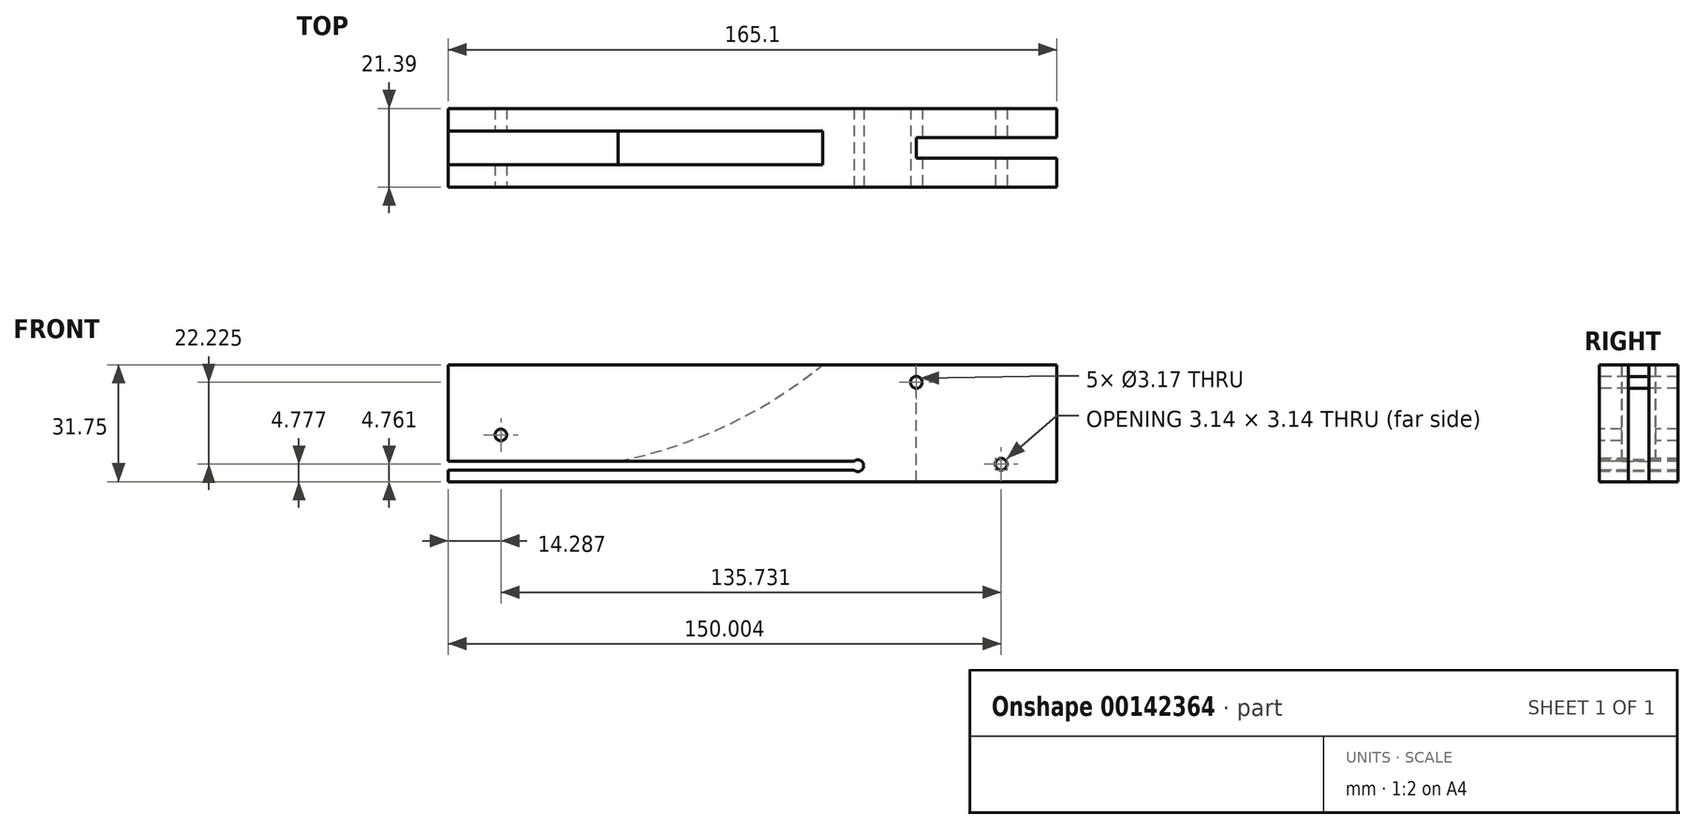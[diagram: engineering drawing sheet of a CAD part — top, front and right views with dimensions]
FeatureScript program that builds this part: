
annotation { "Feature Type Name" : "Feature", "Feature Type Description" : "" }
export const myFeature = defineFeature(function(context is Context, id is Id, definition is map)
    precondition{}
    {
        {
            var Q0;
            Q0=qCreatedBy(makeId("Front.planeOp"),FACE);
            var sketch = newSketch(context, id + "F0", { "sketchPlane" : qUnion([Q0])});
            skPoint(sketch, "E0", {"position": v(-82.55, -12.45) * mm});
            skPoint(sketch, "E1", {"position": v(-57.15, -12.45) * mm});
            skPoint(sketch, "E2", {"position": v(19.05, 16.13) * mm});
            skPoint(sketch, "E3", {"position": v(82.55, 16.13) * mm});
            skPoint(sketch, "E4", {"position": v(82.55, -15.62) * mm});
            skPoint(sketch, "E5", {"position": v(-82.55, -15.62) * mm});
            skLineSegment(sketch, "E6", {"start": v(-82.55, -12.45) * mm, "end": v(-82.55, -15.62) * mm});
            skLineSegment(sketch, "E7", {"start": v(82.55, -15.62) * mm, "end": v(82.55, 16.13) * mm});
            skLineSegment(sketch, "E8", {"start": v(-82.55, -12.45) * mm, "end": v(-57.15, -12.45) * mm});
            skLineSegment(sketch, "E9", {"start": v(-82.55, -15.62) * mm, "end": v(82.55, -15.62) * mm});
            skLineSegment(sketch, "E10", {"start": v(19.05, 16.13) * mm, "end": v(82.55, 16.13) * mm});
            skArc(sketch, "E11", {"start": v(-57.15, -12.45) * mm, "mid": v(-16.7, -4.43) * mm, "end": v(19.05, 16.13) * mm});
            skSolve(sketch);
        }
        {
            var Q0;
            Q0=makeQuery(id+"F0.imprint","IMPRINT",FACE,{"disambiguationData":[TD([[makeQuery(id+"F0.imprint","IMPRINT",EDGE,{"derivedFrom":sQuery(id+"F0.wireOp",EDGE,"E6")}),1.0]])]});
            extrude(context, id + "F1", {"entities" : qUnion([Q0]), "depth" : 9.13 * mm});
        }
        {
            var Q0;
            Q0=makeQuery(id+"F1.opExtrude","CAP_FACE",FACE,{"disambiguationData":[OSD([sQuery(id+"F0.wireOp",EDGE,"E6"),sQuery(id+"F0.wireOp",EDGE,"E7"),sQuery(id+"F0.wireOp",EDGE,"E8"),sQuery(id+"F0.wireOp",EDGE,"E9"),sQuery(id+"F0.wireOp",EDGE,"E10"),sQuery(id+"F0.wireOp",EDGE,"E11")])],"isStart":false});
            var sketch = newSketch(context, id + "F2", { "sketchPlane" : qUnion([Q0])});
            skLineSegment(sketch, "E12", {"start": v(-82.55, -15.62) * mm, "end": v(82.55, -15.62) * mm});
            skLineSegment(sketch, "E13", {"start": v(82.55, -15.62) * mm, "end": v(82.55, 16.13) * mm});
            skLineSegment(sketch, "E14", {"start": v(82.55, 16.13) * mm, "end": v(-82.55, 16.13) * mm});
            skLineSegment(sketch, "E15", {"start": v(-82.55, 16.13) * mm, "end": v(-82.55, -15.62) * mm});
            skSolve(sketch);
        }
        {
            var Q0;
            Q0 = qSketchRegion(id + "F2", true);
            extrude(context, id + "F3", {"entities" : qUnion([Q0]), "operationType" : NewBodyOperationType.ADD, "depth" : 6.13 * mm});
        }
        {
            var Q0;
            Q0=makeQuery(id+"F1.opExtrude","CAP_FACE",FACE,{"disambiguationData":[OSD([sQuery(id+"F0.wireOp",EDGE,"E6"),sQuery(id+"F0.wireOp",EDGE,"E7"),sQuery(id+"F0.wireOp",EDGE,"E8"),sQuery(id+"F0.wireOp",EDGE,"E9"),sQuery(id+"F0.wireOp",EDGE,"E10"),sQuery(id+"F0.wireOp",EDGE,"E11")])],"isStart":true});
            var sketch = newSketch(context, id + "F4", { "sketchPlane" : qUnion([Q0])});
            skLineSegment(sketch, "E16.bottom", {"start": v(-82.55, -15.62) * mm, "end": v(82.55, -15.62) * mm});
            skLineSegment(sketch, "E16.top", {"start": v(-82.55, 16.13) * mm, "end": v(82.55, 16.13) * mm});
            skLineSegment(sketch, "E16.left", {"start": v(-82.55, -15.62) * mm, "end": v(-82.55, 16.13) * mm});
            skLineSegment(sketch, "E16.right", {"start": v(82.55, -15.62) * mm, "end": v(82.55, 16.13) * mm});
            skSolve(sketch);
        }
        {
            var Q0;
            Q0 = qSketchRegion(id + "F4", true);
            extrude(context, id + "F5", {"entities" : qUnion([Q0]), "operationType" : NewBodyOperationType.ADD, "depth" : 6.13 * mm});
        }
        {
            var Q0;
            Q0=makeQuery(id+"F3.opExtrude","CAP_FACE",FACE,{"disambiguationData":[OSD([sQuery(id+"F2.wireOp",EDGE,"E12"),sQuery(id+"F2.wireOp",EDGE,"E13"),sQuery(id+"F2.wireOp",EDGE,"E14"),sQuery(id+"F2.wireOp",EDGE,"E15")])],"isStart":false});
            var sketch = newSketch(context, id + "F6", { "sketchPlane" : qUnion([Q0])});
            skLineSegment(sketch, "E17.bottom", {"start": v(-82.55, -12.45) * mm, "end": v(28.58, -12.45) * mm});
            skLineSegment(sketch, "E17.top", {"start": v(-82.55, -10.06) * mm, "end": v(28.58, -10.06) * mm});
            skLineSegment(sketch, "E17.left", {"start": v(-82.55, -12.45) * mm, "end": v(-82.55, -10.06) * mm});
            skLineSegment(sketch, "E17.right", {"start": v(28.58, -12.45) * mm, "end": v(28.58, -10.06) * mm});
            skSolve(sketch);
        }
        {
            var Q0;
            Q0 = qSketchRegion(id + "F6", true);
            var Q1;
            Q1=makeQuery(id+"F5.opExtrude","CAP_FACE",FACE,{"disambiguationData":[OSD([sQuery(id+"F4.wireOp",EDGE,"E16.bottom"),sQuery(id+"F4.wireOp",EDGE,"E16.top"),sQuery(id+"F4.wireOp",EDGE,"E16.left"),sQuery(id+"F4.wireOp",EDGE,"E16.right")])],"isStart":false});
            extrude(context, id + "F7", {"entities" : qUnion([Q0]), "operationType" : NewBodyOperationType.REMOVE, "endBound" : BoundingType.UP_TO_SURFACE, "oppositeDirection" : true, "endBoundEntityFace" : qUnion([Q1]), "depth" : 25.4 * mm});
        }
        {
            var Q0;
            Q0=makeQuery(id+"F3.opExtrude","CAP_FACE",FACE,{"disambiguationData":[OSD([sQuery(id+"F2.wireOp",EDGE,"E12"),sQuery(id+"F2.wireOp",EDGE,"E13"),sQuery(id+"F2.wireOp",EDGE,"E14"),sQuery(id+"F2.wireOp",EDGE,"E15")])],"isStart":false});
            var sketch = newSketch(context, id + "F8", { "sketchPlane" : qUnion([Q0])});
            skCircle(sketch, "E18", {"center": v(-68.26, -2.92) * mm, "radius": 1.59 * mm});
            skCircle(sketch, "E19", {"center": v(28.58, -11.26) * mm, "radius": 1.59 * mm});
            skCircle(sketch, "E20", {"center": v(44.45, 11.37) * mm, "radius": 1.59 * mm});
            skCircle(sketch, "E21", {"center": v(67.47, -10.86) * mm, "radius": 1.59 * mm});
            skSolve(sketch);
        }
        {
            var Q0;
            Q0 = qSketchRegion(id + "F8", true);
            var Q1;
            Q1=makeQuery(id+"F5.opExtrude","CAP_FACE",FACE,{"disambiguationData":[OSD([sQuery(id+"F4.wireOp",EDGE,"E16.bottom"),sQuery(id+"F4.wireOp",EDGE,"E16.top"),sQuery(id+"F4.wireOp",EDGE,"E16.left"),sQuery(id+"F4.wireOp",EDGE,"E16.right")])],"isStart":false});
            extrude(context, id + "F9", {"entities" : qUnion([Q0]), "operationType" : NewBodyOperationType.REMOVE, "endBound" : BoundingType.UP_TO_SURFACE, "oppositeDirection" : true, "endBoundEntityFace" : qUnion([Q1]), "depth" : 25.4 * mm});
        }
        {
            var Q0;
            Q0=makeQuery(id+"F5.boolean.opBoolean","MERGE",FACE,{"derivedFrom":[makeQuery(id+"F3.boolean.opBoolean","MERGE",FACE,{"derivedFrom":[makeQuery(id+"F1.opExtrude","SWEPT_FACE",FACE,{"disambiguationData":[OSD([sQuery(id+"F0.wireOp",EDGE,"E10")])]}),makeQuery(id+"F3.opExtrude","SWEPT_FACE",FACE,{"disambiguationData":[OSD([sQuery(id+"F2.wireOp",EDGE,"E14")])]})]}),makeQuery(id+"F5.opExtrude","SWEPT_FACE",FACE,{"disambiguationData":[OSD([sQuery(id+"F4.wireOp",EDGE,"E16.top")])]})]});
            var sketch = newSketch(context, id + "F10", { "sketchPlane" : qUnion([Q0])});
            skLineSegment(sketch, "E22.bottom", {"start": v(82.55, -1.79) * mm, "end": v(44.45, -1.79) * mm});
            skLineSegment(sketch, "E22.top", {"start": v(82.55, -7.34) * mm, "end": v(44.45, -7.34) * mm});
            skLineSegment(sketch, "E22.left", {"start": v(82.55, -1.79) * mm, "end": v(82.55, -7.34) * mm});
            skLineSegment(sketch, "E22.right", {"start": v(44.45, -1.79) * mm, "end": v(44.45, -7.34) * mm});
            skPoint(sketch, "E23", {"position": v(82.55, -4.56) * mm});
            skSolve(sketch);
        }
        {
            var Q0;
            Q0 = qSketchRegion(id + "F10", true);
            var Q1;
            Q1=makeQuery(id+"F5.boolean.opBoolean","MERGE",FACE,{"derivedFrom":[makeQuery(id+"F3.boolean.opBoolean","MERGE",FACE,{"derivedFrom":[makeQuery(id+"F1.opExtrude","SWEPT_FACE",FACE,{"disambiguationData":[OSD([sQuery(id+"F0.wireOp",EDGE,"E9")])]}),makeQuery(id+"F3.opExtrude","SWEPT_FACE",FACE,{"disambiguationData":[OSD([sQuery(id+"F2.wireOp",EDGE,"E12")])]})]}),makeQuery(id+"F5.opExtrude","SWEPT_FACE",FACE,{"disambiguationData":[OSD([sQuery(id+"F4.wireOp",EDGE,"E16.bottom")])]})]});
            extrude(context, id + "F11", {"entities" : qUnion([Q0]), "operationType" : NewBodyOperationType.REMOVE, "endBound" : BoundingType.UP_TO_SURFACE, "oppositeDirection" : true, "endBoundEntityFace" : qUnion([Q1]), "depth" : 25.4 * mm});
        }
    });
